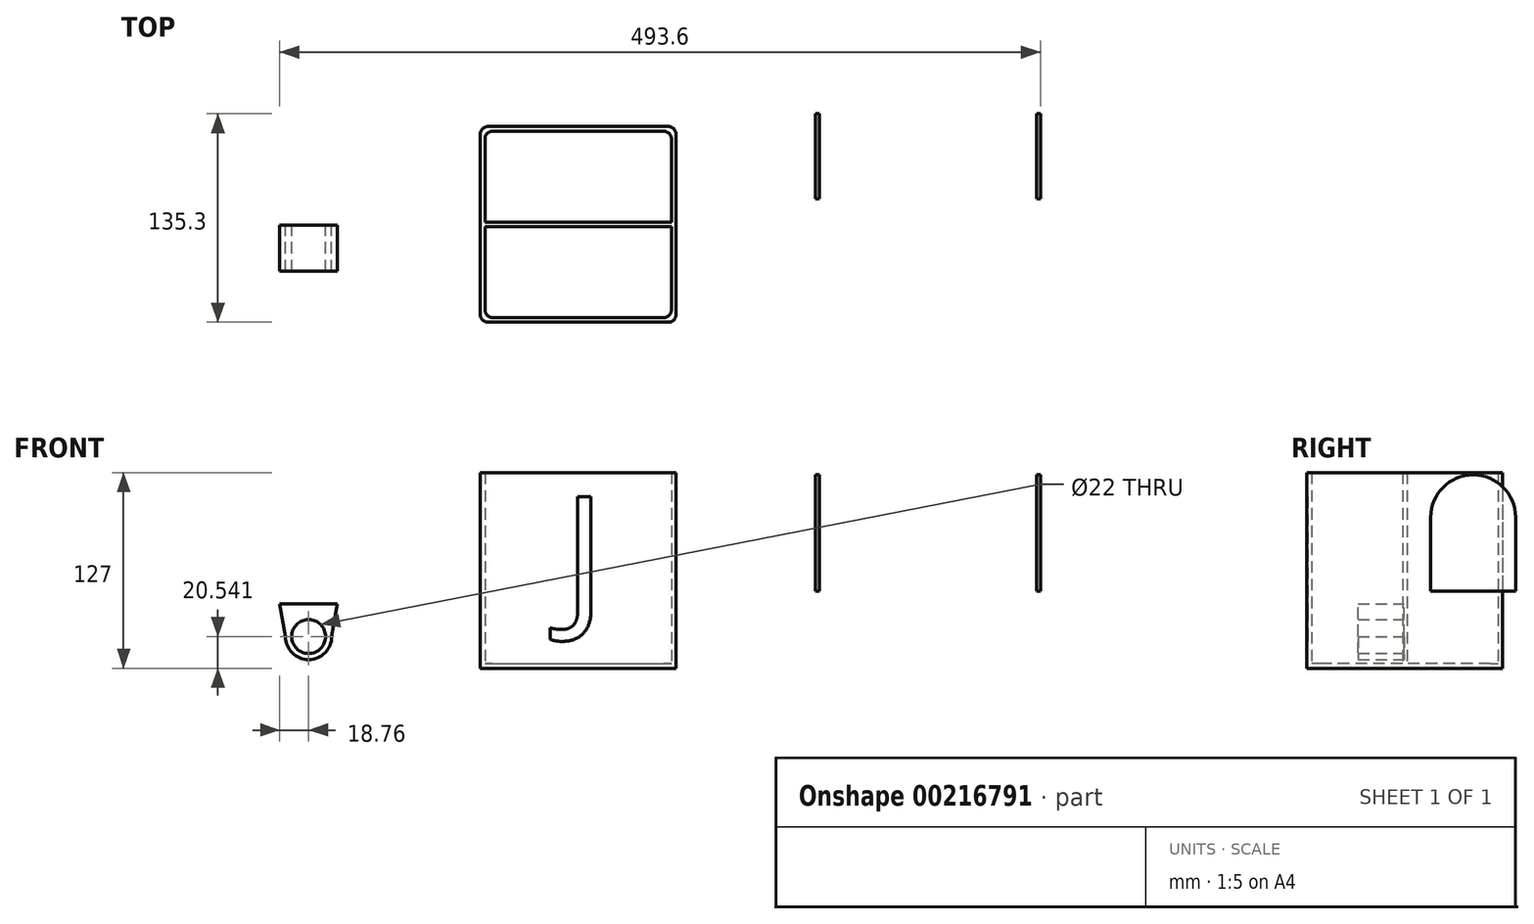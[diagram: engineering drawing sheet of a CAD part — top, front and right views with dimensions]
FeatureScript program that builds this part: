
annotation { "Feature Type Name" : "Feature", "Feature Type Description" : "" }
export const myFeature = defineFeature(function(context is Context, id is Id, definition is map)
    precondition{}
    {
        {
            var Q0;
            Q0=qCreatedBy(makeId("Front.planeOp"),FACE);
            var sketch = newSketch(context, id + "F0", { "sketchPlane" : qUnion([Q0])});
            skLineSegment(sketch, "E0", {"start": v(-93.04, 0) * mm, "end": v(-133.35, 228.6) * mm});
            skLineSegment(sketch, "E1", {"start": v(-133.35, 228.6) * mm, "end": v(-123.35, 228.6) * mm});
            skLineSegment(sketch, "E2", {"start": v(-123.35, 228.6) * mm, "end": v(-84.8, 10) * mm});
            skLineSegment(sketch, "E3", {"start": v(-84.8, 10) * mm, "end": v(0, 10) * mm});
            skLineSegment(sketch, "E4", {"start": v(0, 10) * mm, "end": v(0, 0) * mm});
            skLineSegment(sketch, "E5", {"start": v(0, 0) * mm, "end": v(-93.04, 0) * mm});
            skSolve(sketch);
        }
        {
            var Q0;
            Q0=makeQuery(id+"F0.imprint","IMPRINT",FACE,{"disambiguationData":[TD([[makeQuery(id+"F0.imprint","IMPRINT",EDGE,{"derivedFrom":sQuery(id+"F0.wireOp",EDGE,"E0")}),-1.0]])]});
            var Q1;
            Q1=sQuery(id+"F0.wireOp",EDGE,"E4");
            revolve(context, id + "F1", {"entities" : qUnion([Q0]), "axis" : qUnion([Q1]), "revolveType" : RevolveType.FULL});
        }
        {
            var Q0;
            Q0=makeQuery(id+"F1.opRevolve","SWEPT_EDGE",EDGE,{"disambiguationData":[OSD([sQuery(id+"F0.wireOp",EDGE,"E0"),sQuery(id+"F0.wireOp",EDGE,"E5")])]});
            var Q1;
            Q1=makeQuery(id+"F1.opRevolve","SWEPT_EDGE",EDGE,{"disambiguationData":[OSD([sQuery(id+"F0.wireOp",EDGE,"E0"),sQuery(id+"F0.wireOp",EDGE,"E1")])]});
            var Q2;
            Q2=makeQuery(id+"F1.opRevolve","SWEPT_EDGE",EDGE,{"disambiguationData":[OSD([sQuery(id+"F0.wireOp",EDGE,"E1"),sQuery(id+"F0.wireOp",EDGE,"E2")])]});
            fillet(context, id + "F2", {"entities" : qUnion([Q0, Q1, Q2]), "radius" : 2.5 * mm, "tangentPropagation" : true, "allowEdgeOverflow" : false});
        }
        {
            var Q0;
            Q0=makeQuery(id+"F1.opRevolve","SWEPT_BODY",BODY,{"disambiguationData":[OSD([sQuery(id+"F0.wireOp",EDGE,"E0"),sQuery(id+"F0.wireOp",EDGE,"E1"),sQuery(id+"F0.wireOp",EDGE,"E2"),sQuery(id+"F0.wireOp",EDGE,"E3"),sQuery(id+"F0.wireOp",EDGE,"E4"),sQuery(id+"F0.wireOp",EDGE,"E5")])]});
            deleteBodies(context, id + "F3", {"entities" : qUnion([Q0])});
        }
        {
            var Q0;
            Q0=qCreatedBy(makeId("Top.planeOp"),FACE);
            var sketch = newSketch(context, id + "F4", { "sketchPlane" : qUnion([Q0])});
            skLineSegment(sketch, "E6.bottom", {"start": v(-111.11, 63.91) * mm, "end": v(15.89, 63.91) * mm});
            skLineSegment(sketch, "E6.top", {"start": v(-111.11, -63.09) * mm, "end": v(15.89, -63.09) * mm});
            skLineSegment(sketch, "E6.left", {"start": v(-111.11, 63.91) * mm, "end": v(-111.11, -63.09) * mm});
            skLineSegment(sketch, "E6.right", {"start": v(15.89, 63.91) * mm, "end": v(15.89, -63.09) * mm});
            skSolve(sketch);
        }
        {
            var Q0;
            Q0 = qSketchRegion(id + "F4", true);
            extrude(context, id + "F5", {"entities" : qUnion([Q0]), "depth" : 127 * mm});
        }
        {
            var Q0;
            Q0=makeQuery(id+"F5.opExtrude","CAP_FACE",FACE,{"disambiguationData":[OSD([sQuery(id+"F4.wireOp",EDGE,"E6.bottom"),sQuery(id+"F4.wireOp",EDGE,"E6.top"),sQuery(id+"F4.wireOp",EDGE,"E6.left"),sQuery(id+"F4.wireOp",EDGE,"E6.right")])],"isStart":false});
            shell(context, id + "F6", {"entities" : qUnion([Q0]), "thickness" : 3 * mm});
        }
        {
            var Q0;
            Q0=makeQuery(id+"F6.opShell","OFFSET_EDGE",EDGE,{"disambiguationData":[OSD([sQuery(id+"F4.wireOp",EDGE,"E6.bottom"),sQuery(id+"F4.wireOp",EDGE,"E6.right")])]});
            var Q1;
            Q1=makeQuery(id+"F6.opShell","OFFSET_EDGE",EDGE,{"disambiguationData":[OSD([sQuery(id+"F4.wireOp",EDGE,"E6.bottom"),sQuery(id+"F4.wireOp",EDGE,"E6.left")])]});
            var Q2;
            Q2=makeQuery(id+"F6.opShell","OFFSET_EDGE",EDGE,{"disambiguationData":[OSD([sQuery(id+"F4.wireOp",EDGE,"E6.top"),sQuery(id+"F4.wireOp",EDGE,"E6.right")])]});
            var Q3;
            Q3=makeQuery(id+"F6.opShell","OFFSET_EDGE",EDGE,{"disambiguationData":[OSD([sQuery(id+"F4.wireOp",EDGE,"E6.top"),sQuery(id+"F4.wireOp",EDGE,"E6.left")])]});
            fillet(context, id + "F7", {"entities" : qUnion([Q0, Q1, Q2, Q3]), "radius" : 5 * mm, "tangentPropagation" : true, "allowEdgeOverflow" : false});
        }
        {
            var Q0;
            Q0=makeQuery(id+"F5.opExtrude","SWEPT_EDGE",EDGE,{"disambiguationData":[OSD([sQuery(id+"F4.wireOp",EDGE,"E6.top"),sQuery(id+"F4.wireOp",EDGE,"E6.left")])]});
            var Q1;
            Q1=makeQuery(id+"F5.opExtrude","SWEPT_EDGE",EDGE,{"disambiguationData":[OSD([sQuery(id+"F4.wireOp",EDGE,"E6.top"),sQuery(id+"F4.wireOp",EDGE,"E6.right")])]});
            var Q2;
            Q2=makeQuery(id+"F5.opExtrude","SWEPT_EDGE",EDGE,{"disambiguationData":[OSD([sQuery(id+"F4.wireOp",EDGE,"E6.bottom"),sQuery(id+"F4.wireOp",EDGE,"E6.left")])]});
            var Q3;
            Q3=makeQuery(id+"F5.opExtrude","SWEPT_EDGE",EDGE,{"disambiguationData":[OSD([sQuery(id+"F4.wireOp",EDGE,"E6.bottom"),sQuery(id+"F4.wireOp",EDGE,"E6.right")])]});
            fillet(context, id + "F8", {"entities" : qUnion([Q0, Q1, Q2, Q3]), "radius" : 5 * mm, "tangentPropagation" : true, "allowEdgeOverflow" : false});
        }
        {
            var Q0;
            Q0=makeQuery(id+"F6.opShell","OFFSET_FACE",FACE,{"disambiguationData":[OSD([sQuery(id+"F4.wireOp",EDGE,"E6.bottom"),sQuery(id+"F4.wireOp",EDGE,"E6.top"),sQuery(id+"F4.wireOp",EDGE,"E6.left"),sQuery(id+"F4.wireOp",EDGE,"E6.right")])]});
            var sketch = newSketch(context, id + "F9", { "sketchPlane" : qUnion([Q0])});
            skLineSegment(sketch, "E7.bottom", {"start": v(-108.11, 1.91) * mm, "end": v(12.89, 1.91) * mm});
            skLineSegment(sketch, "E7.top", {"start": v(-108.11, -1.09) * mm, "end": v(12.89, -1.09) * mm});
            skLineSegment(sketch, "E7.left", {"start": v(-108.11, 1.91) * mm, "end": v(-108.11, -1.09) * mm});
            skLineSegment(sketch, "E7.right", {"start": v(12.89, 1.91) * mm, "end": v(12.89, -1.09) * mm});
            skLineSegment(sketch, "E8", {"start": v(-108.11, 0.41) * mm, "end": v(12.89, 0.41) * mm, "construction": true});
            skSolve(sketch);
        }
        {
            var Q0;
            Q0 = qSketchRegion(id + "F9", true);
            extrude(context, id + "F10", {"entities" : qUnion([Q0]), "operationType" : NewBodyOperationType.ADD, "depth" : 124 * mm});
        }
        {
            var Q0;
            Q0=makeQuery(id+"F5.opExtrude","SWEPT_FACE",FACE,{"disambiguationData":[OSD([sQuery(id+"F4.wireOp",EDGE,"E6.top")])]});
            var sketch = newSketch(context, id + "F11", { "sketchPlane" : qUnion([Q0])});
            skLineSegment(sketch, "E9", {"start": v(-47.61, 127) * mm, "end": v(-47.61, 0) * mm, "construction": true});
            skText(sketch, "E10", { "text": "J", "fontName": "OpenSans-Regular.ttf"});
            const initialGuessF11  = {"E10": [-0.05761, 0.037, 1, 0, 0.075]};
            skSetInitialGuess(sketch, initialGuessF11);
            skSolve(sketch);
        }
        {
            var Q0;
            Q0 = qSketchRegion(id + "F11", true);
            extrude(context, id + "F12", {"entities" : qUnion([Q0]), "operationType" : NewBodyOperationType.REMOVE, "oppositeDirection" : true, "depth" : .5 * mm});
        }
        {
            var Q0;
            Q0=qCreatedBy(makeId("Top.planeOp"),FACE);
            var sketch = newSketch(context, id + "F13", { "sketchPlane" : qUnion([Q0])});
            skLineSegment(sketch, "E11.bottom", {"start": v(106.26, 84.21) * mm, "end": v(252.31, 84.21) * mm});
            skLineSegment(sketch, "E11.top", {"start": v(106.26, -61.84) * mm, "end": v(252.31, -61.84) * mm});
            skLineSegment(sketch, "E11.left", {"start": v(106.26, 84.21) * mm, "end": v(106.26, -61.84) * mm});
            skLineSegment(sketch, "E11.right", {"start": v(252.31, 84.21) * mm, "end": v(252.31, -61.84) * mm});
            skSolve(sketch);
        }
        {
            var Q0;
            Q0 = qSketchRegion(id + "F13", true);
            extrude(context, id + "F14", {"entities" : qUnion([Q0]), "depth" : (5.75 * 25.4) * mm});
        }
        {
            var Q0;
            Q0=makeQuery(id+"F14.opExtrude","CAP_FACE",FACE,{"disambiguationData":[OSD([sQuery(id+"F13.wireOp",EDGE,"E11.bottom"),sQuery(id+"F13.wireOp",EDGE,"E11.top"),sQuery(id+"F13.wireOp",EDGE,"E11.left"),sQuery(id+"F13.wireOp",EDGE,"E11.right")])],"isStart":false});
            shell(context, id + "F15", {"entities" : qUnion([Q0]), "thickness" : 2.5 * mm});
        }
        {
            var Q0;
            Q0=makeQuery(id+"F14.opExtrude","SWEPT_FACE",FACE,{"disambiguationData":[OSD([sQuery(id+"F13.wireOp",EDGE,"E11.top")])]});
            var sketch = newSketch(context, id + "F16", { "sketchPlane" : qUnion([Q0])});
            skLineSegment(sketch, "E12.bottom", {"start": v(118.26, 2.5) * mm, "end": v(240.31, 2.5) * mm});
            skLineSegment(sketch, "E12.left", {"start": v(118.26, 2.5) * mm, "end": v(118.26, 77.5) * mm});
            skLineSegment(sketch, "E12.right", {"start": v(240.31, 2.5) * mm, "end": v(240.31, 77.5) * mm});
            skArc(sketch, "E13", {"start": v(240.31, 77.5) * mm, "mid": v(179.29, 138.53) * mm, "end": v(118.26, 77.5) * mm});
            skSolve(sketch);
        }
        {
            var Q0;
            Q0=makeQuery(id+"F16.imprint","IMPRINT",FACE,{"disambiguationData":[TD([[makeQuery(id+"F16.imprint","IMPRINT",EDGE,{"derivedFrom":sQuery(id+"F16.wireOp",EDGE,"E12.bottom")}),1.0]])]});
            extrude(context, id + "F17", {"entities" : qUnion([Q0]), "operationType" : NewBodyOperationType.REMOVE, "oppositeDirection" : true, "depth" : 25 * mm});
        }
        {
            var Q0;
            Q0=makeQuery(id+"F14.opExtrude","SWEPT_FACE",FACE,{"disambiguationData":[OSD([sQuery(id+"F13.wireOp",EDGE,"E11.right")])]});
            var sketch = newSketch(context, id + "F18", { "sketchPlane" : qUnion([Q0])});
            skLineSegment(sketch, "E14", {"start": v(11.19, 146.05) * mm, "end": v(11.19, 0) * mm, "construction": true});
            skLineSegment(sketch, "E15.top", {"start": v(-49.84, 50) * mm, "end": v(5.19, 50) * mm});
            skLineSegment(sketch, "E15.left", {"start": v(-49.84, 98) * mm, "end": v(-49.84, 50) * mm});
            skLineSegment(sketch, "E15.right", {"start": v(5.19, 98) * mm, "end": v(5.19, 50) * mm});
            skArc(sketch, "E16", {"start": v(5.19, 98) * mm, "mid": v(-22.32, 125.51) * mm, "end": v(-49.84, 98) * mm});
            skArc(sketch, "E17.MirrorCS", {"start": v(17.19, 98) * mm, "mid": v(44.7, 125.51) * mm, "end": v(72.21, 98) * mm});
            skLineSegment(sketch, "E18.MirrorCS", {"start": v(17.19, 98) * mm, "end": v(17.19, 50) * mm});
            skLineSegment(sketch, "E19.MirrorCS", {"start": v(72.21, 50) * mm, "end": v(17.19, 50) * mm});
            skLineSegment(sketch, "E20.MirrorCS", {"start": v(72.21, 98) * mm, "end": v(72.21, 50) * mm});
            skSolve(sketch);
        }
        {
            var Q0;
            Q0=makeQuery(id+"F18.imprint","IMPRINT",FACE,{"disambiguationData":[TD([[makeQuery(id+"F18.imprint","IMPRINT",EDGE,{"derivedFrom":sQuery(id+"F18.wireOp",EDGE,"E15.top")}),1.0]])]});
            var Q1;
            Q1=makeQuery(id+"F18.imprint","IMPRINT",FACE,{"disambiguationData":[TD([[makeQuery(id+"F18.imprint","IMPRINT",EDGE,{"derivedFrom":sQuery(id+"F18.wireOp",EDGE,"E17.MirrorCS")}),-1.0]])]});
            extrude(context, id + "F19", {"entities" : qUnion([Q0, Q1]), "operationType" : NewBodyOperationType.REMOVE, "oppositeDirection" : true, "depth" : 168 * mm, "offsetDistance" : 25 * mm});
        }
        {
            var Q0;
            Q0=qCreatedBy(makeId("Front.planeOp"),FACE);
            var sketch = newSketch(context, id + "F20", { "sketchPlane" : qUnion([Q0])});
            skArc(sketch, "E21", {"start": v(-237.53, 20.54) * mm, "mid": v(-222.53, 5.54) * mm, "end": v(-207.53, 20.54) * mm});
            skCircle(sketch, "E22", {"center": v(-222.53, 20.54) * mm, "radius": 11 * mm});
            skLineSegment(sketch, "E23", {"start": v(-237.53, 20.54) * mm, "end": v(-241.29, 41.86) * mm});
            skLineSegment(sketch, "E24", {"start": v(-222.53, 20.54) * mm, "end": v(-222.53, 70.78) * mm, "construction": true});
            skLineSegment(sketch, "E25.MirrorCS", {"start": v(-207.53, 20.54) * mm, "end": v(-203.77, 41.86) * mm});
            skLineSegment(sketch, "E26", {"start": v(-241.29, 41.86) * mm, "end": v(-203.77, 41.86) * mm});
            skSolve(sketch);
        }
        {
            var Q0;
            Q0 = qSketchRegion(id + "F20", true);
            extrude(context, id + "F21", {"entities" : qUnion([Q0]), "depth" : 30 * mm, "offsetDistance" : 25 * mm});
        }
    });
